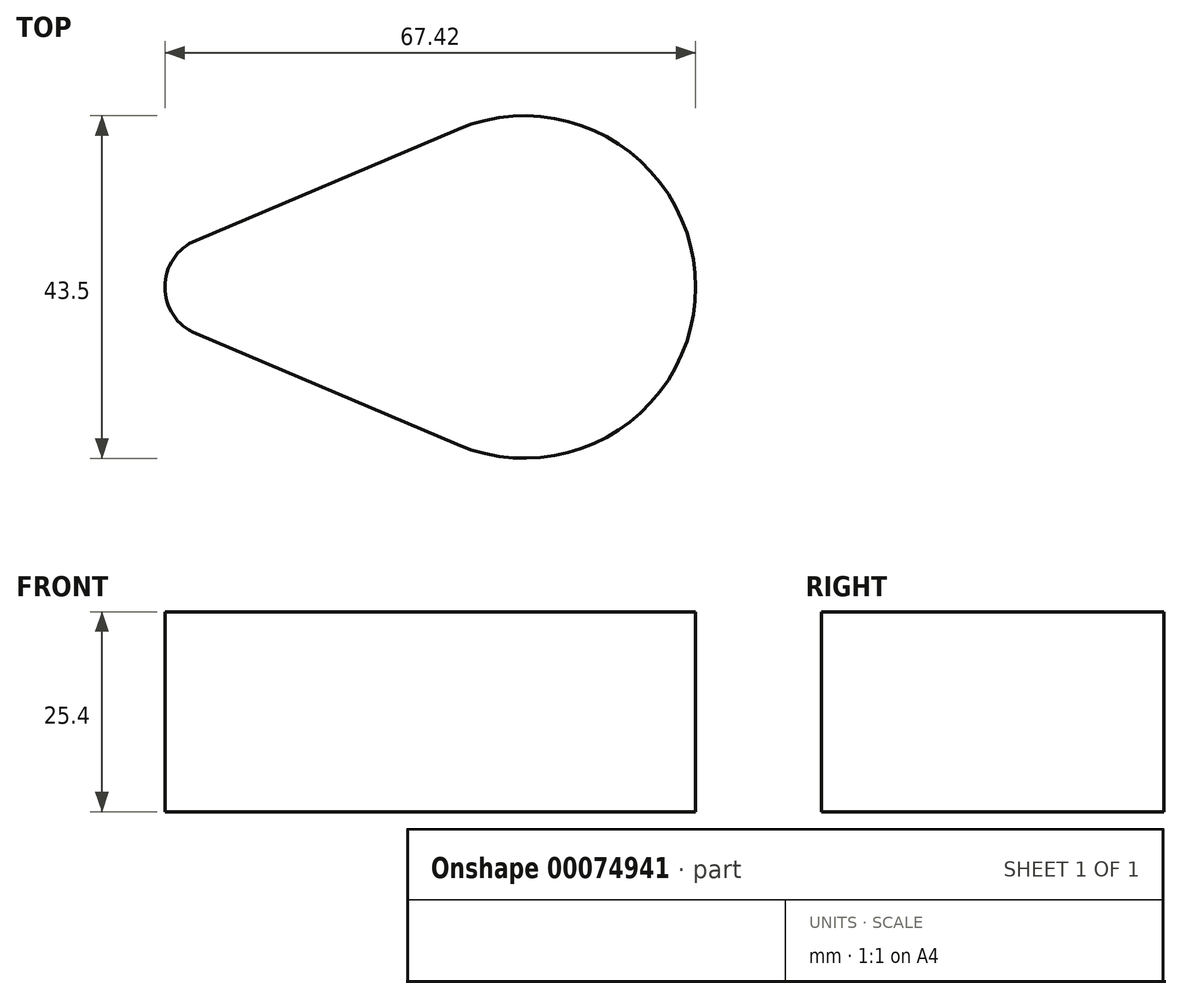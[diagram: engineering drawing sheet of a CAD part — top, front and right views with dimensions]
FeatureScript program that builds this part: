
annotation { "Feature Type Name" : "Feature", "Feature Type Description" : "" }
export const myFeature = defineFeature(function(context is Context, id is Id, definition is map)
    precondition{}
    {
        {
            var Q0;
            Q0=qCreatedBy(makeId("Top.planeOp"),FACE);
            var sketch = newSketch(context, id + "F0", { "sketchPlane" : qUnion([Q0])});
            skArc(sketch, "E0", {"start": v(-41.74, 5.93) * mm, "mid": v(-45.67, 0) * mm, "end": v(-41.74, -5.93) * mm});
            skArc(sketch, "E1", {"start": v(-8.49, -20.03) * mm, "mid": v(21.75, 0) * mm, "end": v(-8.49, 20.03) * mm});
            skLineSegment(sketch, "E2", {"start": v(-41.74, 5.93) * mm, "end": v(-8.49, 20.03) * mm});
            skLineSegment(sketch, "E3.MirrorCS", {"start": v(-41.74, -5.93) * mm, "end": v(-8.49, -20.03) * mm});
            skSolve(sketch);
        }
        {
            var Q0;
            Q0 = qSketchRegion(id + "F0", true);
            extrude(context, id + "F1", {"entities" : qUnion([Q0]), "depth" : 25.4 * mm});
        }
    });
